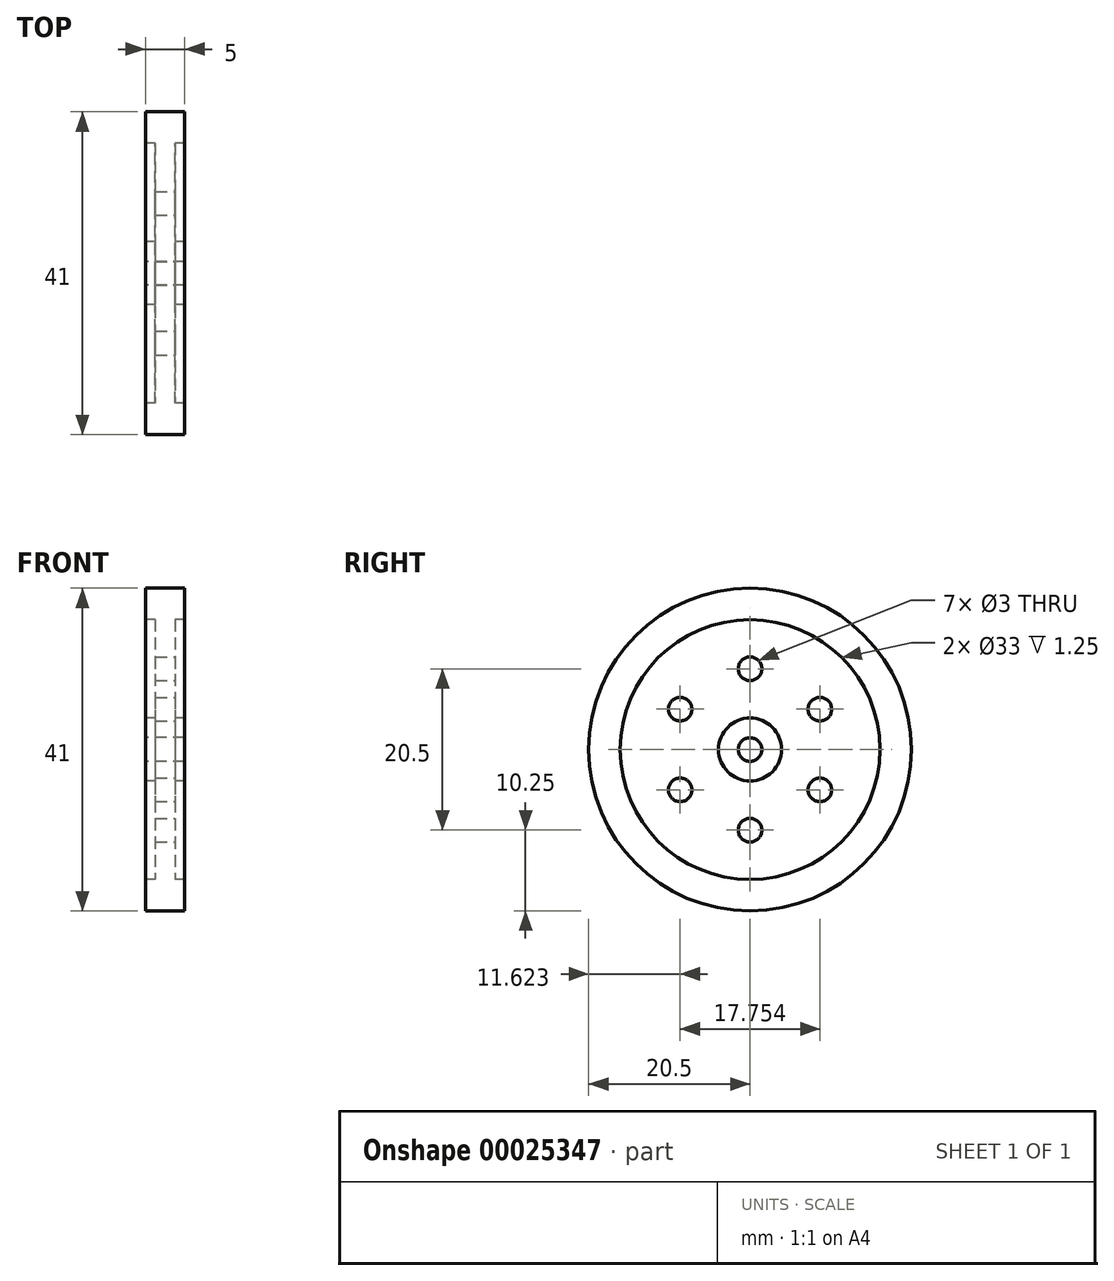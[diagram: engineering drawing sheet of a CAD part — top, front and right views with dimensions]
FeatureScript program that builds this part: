
annotation { "Feature Type Name" : "Feature", "Feature Type Description" : "" }
export const myFeature = defineFeature(function(context is Context, id is Id, definition is map)
    precondition{}
    {
        {
            var Q0;
            Q0=qCreatedBy(makeId("Front.planeOp"),FACE);
            var sketch = newSketch(context, id + "F0", { "sketchPlane" : qUnion([Q0])});
            skLineSegment(sketch, "E0", {"start": v(-50.28, 0) * mm, "end": v(50.2, 0) * mm, "construction": true});
            skLineSegment(sketch, "E1.rect.bottom", {"start": v(2.5, 4) * mm, "end": v(-2.5, 4) * mm});
            skLineSegment(sketch, "E1.rect.top", {"start": v(2.5, 1.5) * mm, "end": v(-2.5, 1.5) * mm});
            skLineSegment(sketch, "E1.rect.left", {"start": v(2.5, 4) * mm, "end": v(2.5, 1.5) * mm});
            skLineSegment(sketch, "E1.rect.right", {"start": v(-2.5, 4) * mm, "end": v(-2.5, 1.5) * mm});
            skPoint(sketch, "E1.rect.middle", {"position": v(0, 2.75) * mm});
            skLineSegment(sketch, "E2.bottom", {"start": v(-1.25, 4) * mm, "end": v(1.25, 4) * mm});
            skLineSegment(sketch, "E2.top", {"start": v(-1.25, 16.5) * mm, "end": v(1.25, 16.5) * mm});
            skLineSegment(sketch, "E2.left", {"start": v(-1.25, 4) * mm, "end": v(-1.25, 16.5) * mm});
            skLineSegment(sketch, "E2.right", {"start": v(1.25, 4) * mm, "end": v(1.25, 16.5) * mm});
            skLineSegment(sketch, "E3.rect.bottom", {"start": v(2.5, 16.5) * mm, "end": v(-2.5, 16.5) * mm});
            skLineSegment(sketch, "E3.rect.top", {"start": v(2.5, 20.5) * mm, "end": v(-2.5, 20.5) * mm});
            skLineSegment(sketch, "E3.rect.left", {"start": v(2.5, 16.5) * mm, "end": v(2.5, 20.5) * mm});
            skLineSegment(sketch, "E3.rect.right", {"start": v(-2.5, 16.5) * mm, "end": v(-2.5, 20.5) * mm});
            skPoint(sketch, "E3.rect.middle", {"position": v(0, 18.5) * mm});
            skSolve(sketch);
        }
        {
            var Q0;
            Q0=qSketchRegion(id+"F0",true);
            var Q1;
            Q1=sQuery(id+"F0.wireOp",EDGE,"E0");
            revolve(context, id + "F1", {"entities" : qUnion([Q0]), "axis" : qUnion([Q1]), "revolveType" : RevolveType.FULL});
        }
        {
            var Q0;
            Q0=makeQuery(id+"F1.opRevolve","SWEPT_FACE",FACE,{"disambiguationData":[OSD([sQuery(id+"F0.wireOp",EDGE,"E3.rect.left")])]});
            var sketch = newSketch(context, id + "F2", { "sketchPlane" : qUnion([Q0])});
            skLineSegment(sketch, "E4", {"start": v(0, 0) * mm, "end": v(0, 20.5) * mm, "construction": true});
            skLineSegment(sketch, "E5", {"start": v(0, 20.5) * mm, "end": v(0, 0) * mm, "construction": true});
            skLineSegment(sketch, "E6", {"start": v(0, 0) * mm, "end": v(0, -20.5) * mm, "construction": true});
            skLineSegment(sketch, "E7", {"start": v(0, -20.5) * mm, "end": v(0, 0) * mm, "construction": true});
            skLineSegment(sketch, "E8", {"start": v(0, 0) * mm, "end": v(17.75, 10.25) * mm, "construction": true});
            skLineSegment(sketch, "E9", {"start": v(17.75, 10.25) * mm, "end": v(-17.75, -10.25) * mm, "construction": true});
            skLineSegment(sketch, "E10", {"start": v(0, 0) * mm, "end": v(17.75, -10.25) * mm, "construction": true});
            skLineSegment(sketch, "E11", {"start": v(17.75, -10.25) * mm, "end": v(-17.75, 10.25) * mm, "construction": true});
            skPoint(sketch, "E12", {"position": v(0, 10.25) * mm});
            skCircle(sketch, "E13", {"center": v(0, 0) * mm, "radius": 10.25 * mm, "construction": true});
            skCircle(sketch, "E14", {"center": v(0, 10.25) * mm, "radius": 1.5 * mm});
            skCircle(sketch, "E15", {"center": v(8.88, 5.13) * mm, "radius": 1.5 * mm});
            skCircle(sketch, "E16", {"center": v(8.88, -5.12) * mm, "radius": 1.5 * mm});
            skCircle(sketch, "E17", {"center": v(0, -10.25) * mm, "radius": 1.5 * mm});
            skCircle(sketch, "E18", {"center": v(-8.88, -5.13) * mm, "radius": 1.5 * mm});
            skCircle(sketch, "E19", {"center": v(-8.88, 5.12) * mm, "radius": 1.5 * mm});
            skSolve(sketch);
        }
        {
            var Q0;
            Q0=qSketchRegion(id+"F2",true);
            extrude(context, id + "F3", {"entities" : qUnion([Q0]), "operationType" : NewBodyOperationType.REMOVE, "oppositeDirection" : true, "depth" : 25 * mm});
        }
    });
